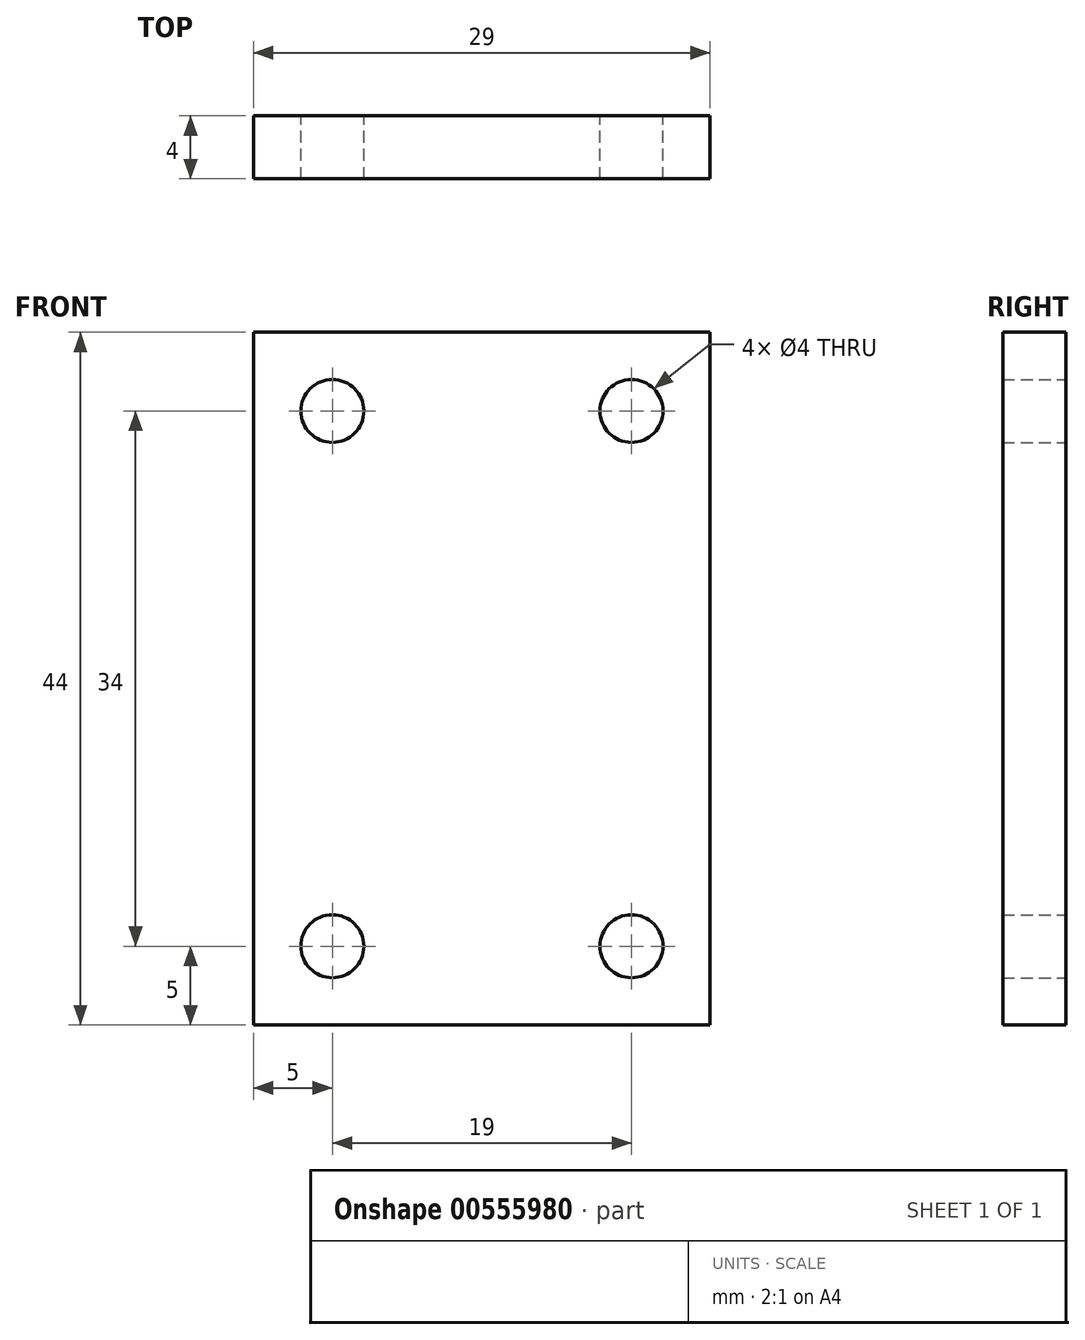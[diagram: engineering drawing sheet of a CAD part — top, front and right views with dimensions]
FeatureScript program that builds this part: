
annotation { "Feature Type Name" : "Feature", "Feature Type Description" : "" }
export const myFeature = defineFeature(function(context is Context, id is Id, definition is map)
    precondition{}
    {
        {
            assignVariable(context, id + "F0", {"name" : "thickness", "anyValue" : 4});
        }
        {
            var Q0;
            Q0=qCreatedBy(makeId("Front.planeOp"),FACE);
            var sketch = newSketch(context, id + "F1", { "sketchPlane" : qUnion([Q0])});
            skLineSegment(sketch, "E0.bottom", {"start": v(-14.5, 22) * mm, "end": v(14.5, 22) * mm});
            skLineSegment(sketch, "E0.top", {"start": v(-14.5, -22) * mm, "end": v(14.5, -22) * mm});
            skLineSegment(sketch, "E0.left", {"start": v(-14.5, 22) * mm, "end": v(-14.5, -22) * mm});
            skLineSegment(sketch, "E0.right", {"start": v(14.5, 22) * mm, "end": v(14.5, -22) * mm});
            skPoint(sketch, "E0.middle", {"position": v(0, 0) * mm});
            skCircle(sketch, "E1", {"center": v(-9.5, 17) * mm, "radius": 2 * mm});
            skCircle(sketch, "E2", {"center": v(9.5, 17) * mm, "radius": 2 * mm});
            skCircle(sketch, "E3", {"center": v(-9.5, -17) * mm, "radius": 2 * mm});
            skCircle(sketch, "E4", {"center": v(9.5, -17) * mm, "radius": 2 * mm});
            skSolve(sketch);
        }
        {
            var Q0;
            Q0 = qSketchRegion(id + "F1", true);
            extrude(context, id + "F2", {"entities" : qUnion([Q0]), "depth" : (getVariable(context, 'thickness')) * mm, "offsetDistance" : 25 * mm});
        }
    });
